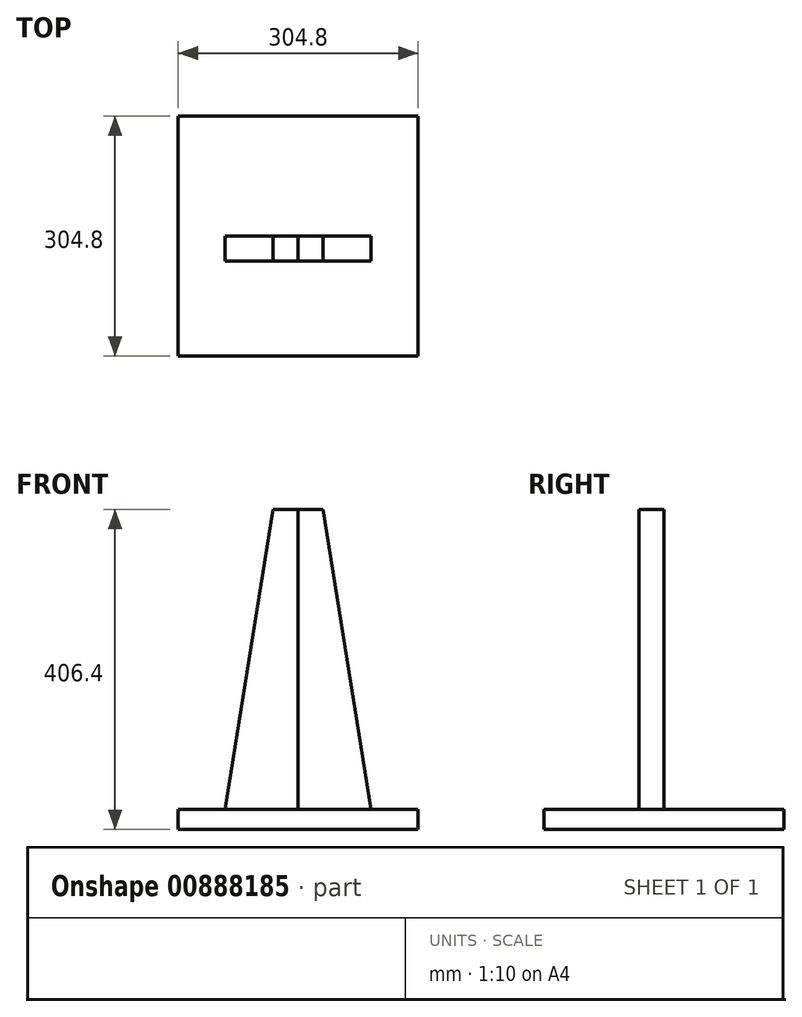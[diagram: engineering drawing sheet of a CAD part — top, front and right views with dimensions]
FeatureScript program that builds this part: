
annotation { "Feature Type Name" : "Feature", "Feature Type Description" : "" }
export const myFeature = defineFeature(function(context is Context, id is Id, definition is map)
    precondition{}
    {
        {
            var Q0;
            Q0=qCreatedBy(makeId("Top.planeOp"),FACE);
            var sketch = newSketch(context, id + "F0", { "sketchPlane" : qUnion([Q0])});
            skLineSegment(sketch, "E0.bottom", {"start": v(152.4, 152.4) * mm, "end": v(-152.4, 152.4) * mm});
            skLineSegment(sketch, "E0.top", {"start": v(152.4, -152.4) * mm, "end": v(-152.4, -152.4) * mm});
            skLineSegment(sketch, "E0.left", {"start": v(152.4, 152.4) * mm, "end": v(152.4, -152.4) * mm});
            skLineSegment(sketch, "E0.right", {"start": v(-152.4, 152.4) * mm, "end": v(-152.4, -152.4) * mm});
            skPoint(sketch, "E0.middle", {"position": v(0, 0) * mm});
            skSolve(sketch);
        }
        {
            var Q0;
            Q0=qSketchRegion(id+"F0",true);
            extrude(context, id + "F1", {"entities" : qUnion([Q0]), "depth" : 25.4 * mm, "offsetDistance" : 25.4 * mm});
        }
        {
            var Q0;
            Q0=qCreatedBy(makeId("Front.planeOp"),FACE);
            var sketch = newSketch(context, id + "F2", { "sketchPlane" : qUnion([Q0])});
            skLineSegment(sketch, "E1", {"start": v(-92.74, 25.4) * mm, "end": v(-31.78, 406.4) * mm});
            skLineSegment(sketch, "E2", {"start": v(-31.78, 406.4) * mm, "end": v(0, 406.4) * mm});
            skLineSegment(sketch, "E3", {"start": v(0, 406.4) * mm, "end": v(-0.15, 25.4) * mm});
            skLineSegment(sketch, "E4", {"start": v(-0.15, 25.4) * mm, "end": v(-92.74, 25.4) * mm});
            skSolve(sketch);
        }
        {
            var Q0;
            Q0=qCreatedBy(makeId("Front.planeOp"),FACE);
            var sketch = newSketch(context, id + "F3", { "sketchPlane" : qUnion([Q0])});
            skLineSegment(sketch, "E5", {"start": v(92.44, 25.4) * mm, "end": v(31.48, 406.4) * mm});
            skLineSegment(sketch, "E6", {"start": v(-0.3, 406.4) * mm, "end": v(31.48, 406.4) * mm});
            skLineSegment(sketch, "E7", {"start": v(-0.3, 406.4) * mm, "end": v(-0.15, 25.4) * mm});
            skLineSegment(sketch, "E8", {"start": v(92.44, 25.4) * mm, "end": v(-0.15, 25.4) * mm});
            skSolve(sketch);
        }
        {
            var Q0;
            Q0=makeQuery(id+"F3.imprint","IMPRINT",FACE,{"disambiguationData":[TD([[makeQuery(id+"F3.imprint","IMPRINT",EDGE,{"derivedFrom":sQuery(id+"F3.wireOp",EDGE,"E5")}),1.0]])]});
            var Q1;
            Q1=makeQuery(id+"F2.imprint","IMPRINT",FACE,{"disambiguationData":[TD([[makeQuery(id+"F2.imprint","IMPRINT",EDGE,{"derivedFrom":sQuery(id+"F2.wireOp",EDGE,"E1")}),-1.0]])]});
            extrude(context, id + "F4", {"entities" : qUnion([Q0, Q1]), "depth" : 31.75 * mm, "offsetDistance" : 25.4 * mm});
        }
    });
